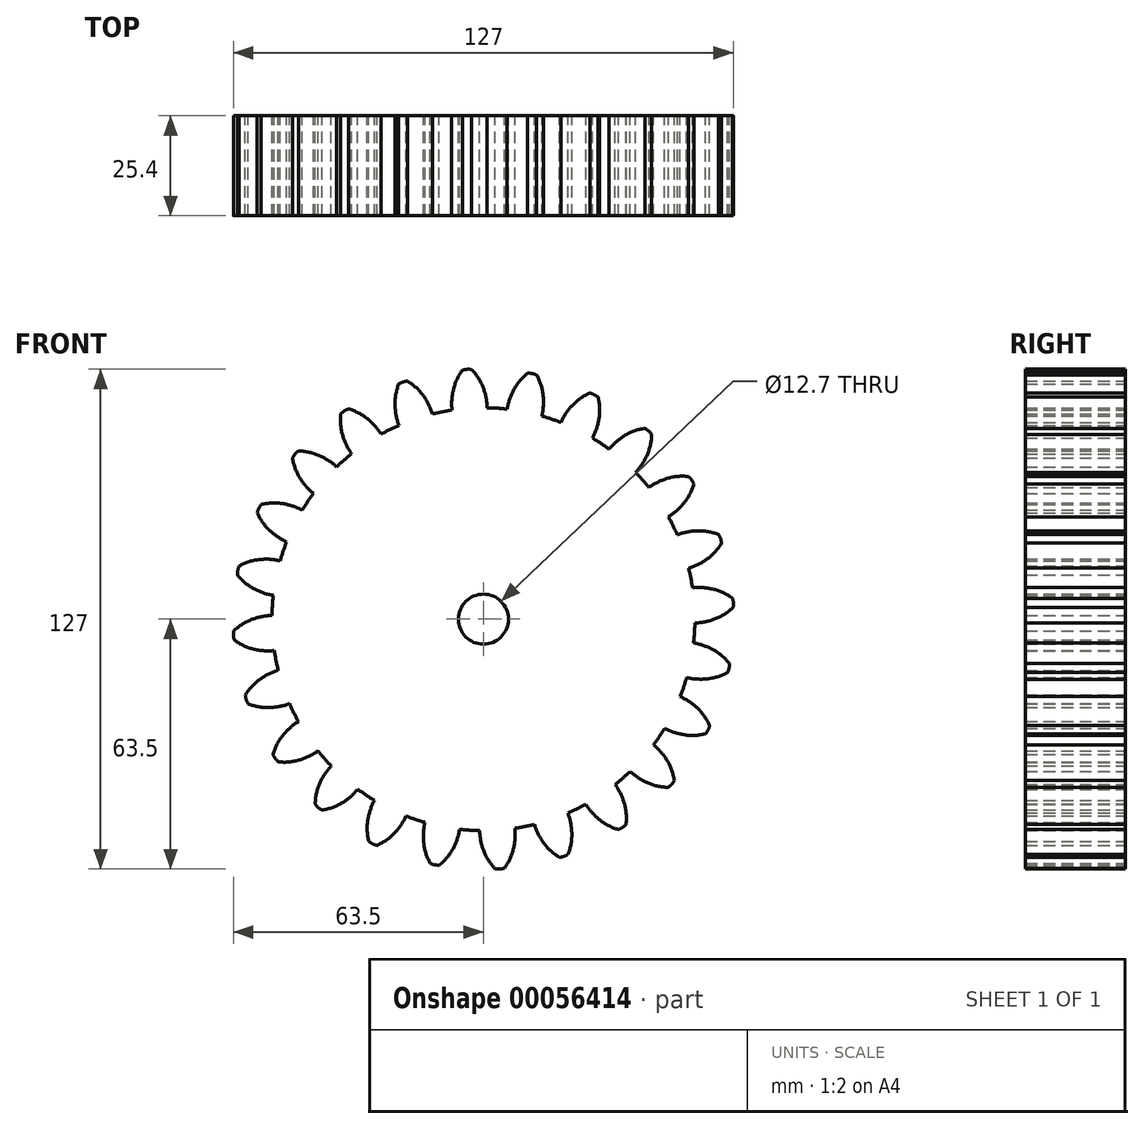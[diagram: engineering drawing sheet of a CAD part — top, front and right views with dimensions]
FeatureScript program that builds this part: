
annotation { "Feature Type Name" : "Feature", "Feature Type Description" : "" }
export const myFeature = defineFeature(function(context is Context, id is Id, definition is map)
    precondition{}
    {
        {
            var Q0;
            Q0=qCreatedBy(makeId("Front.planeOp"),FACE);
            var sketch = newSketch(context, id + "F0", { "sketchPlane" : qUnion([Q0])});
            skCircle(sketch, "E0", {"center": v(0, 0) * mm, "radius": 53.72 * mm});
            skCircle(sketch, "E1", {"center": v(0, 0) * mm, "radius": 58.67 * mm, "construction": true});
            skCircle(sketch, "E2", {"center": v(0, 0) * mm, "radius": 63.5 * mm, "construction": true});
            skLineSegment(sketch, "E3", {"start": v(0, 0) * mm, "end": v(0, 120.5) * mm, "construction": true});
            skLineSegment(sketch, "E4", {"start": v(0, 0) * mm, "end": v(-7.89, 120.3) * mm, "construction": true});
            skLineSegment(sketch, "E5", {"start": v(0, 58.67) * mm, "end": v(-147.93, 58.67) * mm, "construction": true});
            skLineSegment(sketch, "E6", {"start": v(0, 58.67) * mm, "end": v(-142.92, 6.66) * mm, "construction": true});
            skCircle(sketch, "E7", {"center": v(0, 0) * mm, "radius": 55.14 * mm, "construction": true});
            skCircle(sketch, "E8", {"center": v(0, 58.67) * mm, "radius": 14.6 * mm, "construction": true});
            skCircle(sketch, "E9", {"center": v(-13.63, 53.42) * mm, "radius": 14.6 * mm, "construction": true});
            skArc(sketch, "E10", {"start": v(0, 58.67) * mm, "mid": v(-1.25, 61.2) * mm, "end": v(-2.99, 63.43) * mm});
            skArc(sketch, "E11", {"start": v(0.97, 53.71) * mm, "mid": v(0.69, 56.23) * mm, "end": v(0, 58.67) * mm});
            skArc(sketch, "E12.MirrorCS", {"start": v(-7.66, 58.17) * mm, "mid": v(-6.75, 60.85) * mm, "end": v(-5.32, 63.28) * mm});
            skArc(sketch, "E13.MirrorCS", {"start": v(-7.98, 53.13) * mm, "mid": v(-8.02, 55.66) * mm, "end": v(-7.66, 58.17) * mm});
            skArc(sketch, "E14", {"start": v(-2.99, 63.43) * mm, "mid": v(-4.16, 63.5) * mm, "end": v(-5.32, 63.28) * mm});
            skCircle(sketch, "E15", {"center": v(0, 0) * mm, "radius": 6.35 * mm});
            skSolve(sketch);
        }
        {
            var Q0;
            Q0=makeQuery(id+"F0.imprint","IMPRINT",FACE,{"disambiguationData":[TD([[makeQuery(id+"F0.imprint","IMPRINT",EDGE,{"derivedFrom":sQuery(id+"F0.wireOp",EDGE,"E10")}),1.0]])]});
            var Q1;
            {var subQ0=sQuery(id+"F0.wireOp",EDGE,"E0");var subQ1=makeQuery(id+"F0.imprint","INTERSECT",VERTEX,{"derivedFrom":[subQ0,sQuery(id+"F0.wireOp",EDGE,"E11")]});Q1=makeQuery(id+"F0.imprint","IMPRINT",FACE,{"disambiguationData":[TD([[makeQuery(id+"F0.imprint","IMPRINT",EDGE,{"disambiguationData":[TD([[subQ1,-1.0]])],"derivedFrom":subQ0}),1.0]])]});}
            extrude(context, id + "F1", {"entities" : qUnion([Q0, Q1]), "depth" : 25.4 * mm});
        }
        {
            var Q0;
            Q0=makeQuery(id+"F1.opExtrude","SWEPT_BODY",BODY,{"disambiguationData":[OSD([sQuery(id+"F0.wireOp",EDGE,"E0"),sQuery(id+"F0.wireOp",EDGE,"E10"),sQuery(id+"F0.wireOp",EDGE,"E11"),sQuery(id+"F0.wireOp",EDGE,"E12.MirrorCS"),sQuery(id+"F0.wireOp",EDGE,"E13.MirrorCS"),sQuery(id+"F0.wireOp",EDGE,"E14")])]});
            var Q1;
            Q1=makeQuery(id+"F1.opExtrude","SWEPT_FACE",FACE,{"disambiguationData":[OSD([sQuery(id+"F0.wireOp",EDGE,"E0")])]});
            circularPattern(context, id + "F2", {"operationType" : NewBodyOperationType.ADD, "entities" : qUnion([Q0]), "axis" : qUnion([Q1]), "angle" : 15 * degree, "instanceCount" : round(24)});
        }
    });
